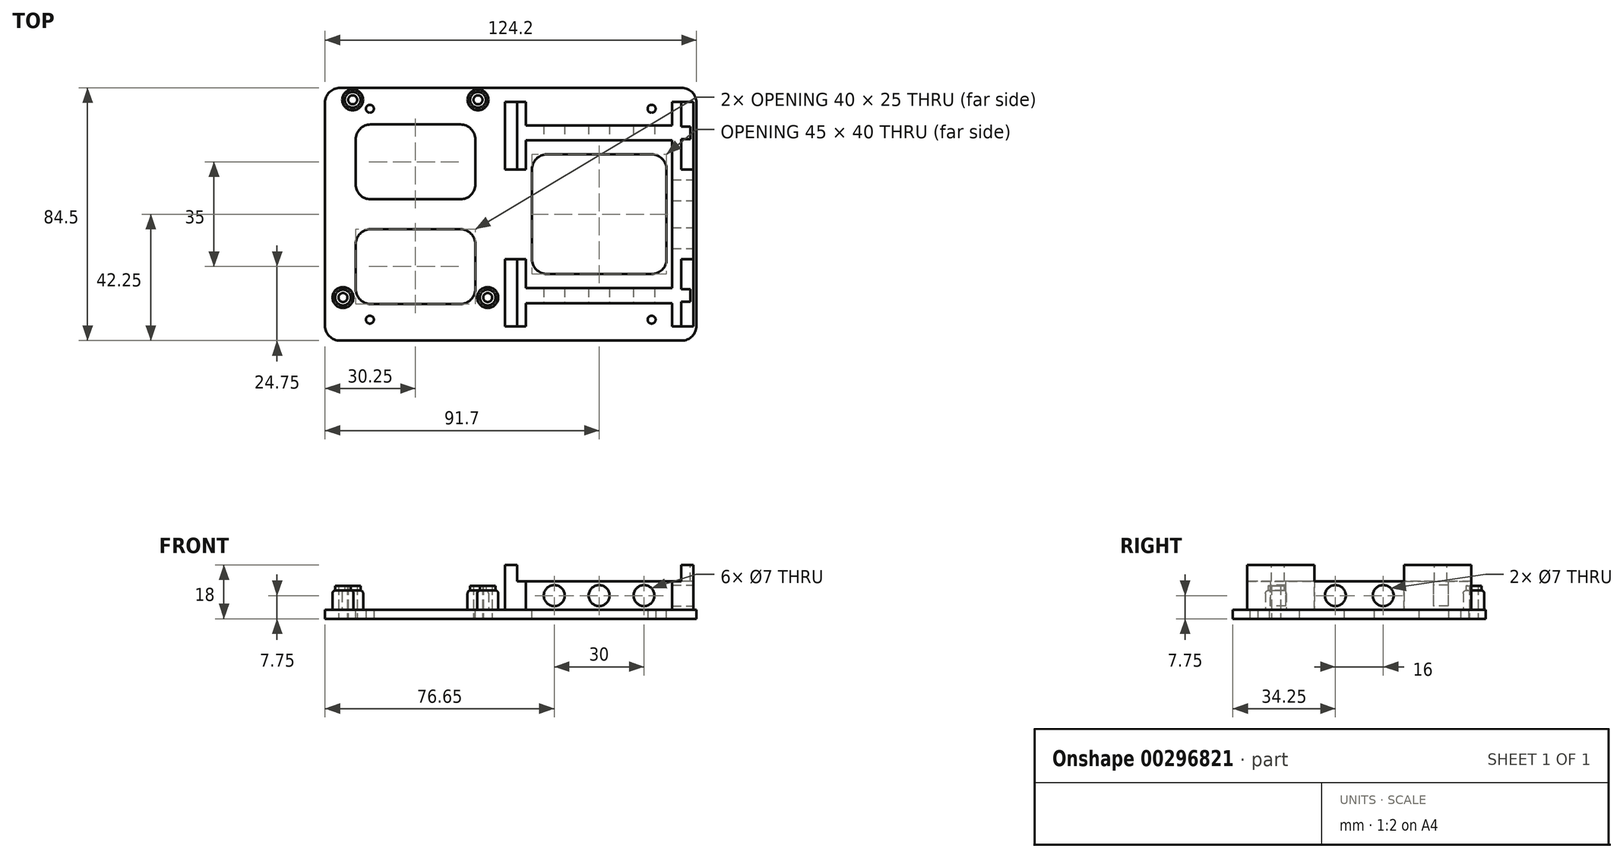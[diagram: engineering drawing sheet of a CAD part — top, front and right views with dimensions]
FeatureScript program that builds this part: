
annotation { "Feature Type Name" : "Feature", "Feature Type Description" : "" }
export const myFeature = defineFeature(function(context is Context, id is Id, definition is map)
    precondition{}
    {
        {
            var Q0;
            Q0=qCreatedBy(makeId("Top.planeOp"),FACE);
            var sketch = newSketch(context, id + "F0", { "sketchPlane" : qUnion([Q0])});
            skLineSegment(sketch, "E0", {"start": v(0, 0) * mm, "end": v(0, 35.25) * mm, "construction": true});
            skLineSegment(sketch, "E1", {"start": v(0, 35.25) * mm, "end": v(47.1, 35.25) * mm, "construction": true});
            skLineSegment(sketch, "E2", {"start": v(47.1, 35.25) * mm, "end": v(47.1, 0) * mm, "construction": true});
            skLineSegment(sketch, "E3", {"start": v(47.1, 0) * mm, "end": v(47.1, -35.25) * mm, "construction": true});
            skLineSegment(sketch, "E4", {"start": v(47.1, -35.25) * mm, "end": v(0, -35.25) * mm, "construction": true});
            skLineSegment(sketch, "E5", {"start": v(0, -35.25) * mm, "end": v(-47.1, -35.25) * mm, "construction": true});
            skLineSegment(sketch, "E6", {"start": v(-47.1, -35.25) * mm, "end": v(-47.1, 0) * mm, "construction": true});
            skLineSegment(sketch, "E7", {"start": v(-47.1, 0) * mm, "end": v(-47.1, 35.25) * mm, "construction": true});
            skLineSegment(sketch, "E8", {"start": v(-47.1, 35.25) * mm, "end": v(0, 35.25) * mm, "construction": true});
            skLineSegment(sketch, "E9", {"start": v(0, 0) * mm, "end": v(0, -35.25) * mm, "construction": true});
            skLineSegment(sketch, "E10", {"start": v(0, 0) * mm, "end": v(47.1, 0) * mm, "construction": true});
            skLineSegment(sketch, "E11", {"start": v(0, 0) * mm, "end": v(-47.1, 0) * mm, "construction": true});
            skCircle(sketch, "E12", {"center": v(-47.1, 35.25) * mm, "radius": 1.32 * mm});
            skCircle(sketch, "E13", {"center": v(-47.1, -35.25) * mm, "radius": 1.32 * mm});
            skCircle(sketch, "E14", {"center": v(47.1, -35.25) * mm, "radius": 1.32 * mm});
            skCircle(sketch, "E15", {"center": v(47.1, 35.25) * mm, "radius": 1.32 * mm});
            skLineSegment(sketch, "E16", {"start": v(0, 35.25) * mm, "end": v(0, 42.25) * mm, "construction": true});
            skLineSegment(sketch, "E17", {"start": v(0, -35.25) * mm, "end": v(0, -42.25) * mm, "construction": true});
            skLineSegment(sketch, "E18", {"start": v(0, 42.25) * mm, "end": v(57.1, 42.25) * mm});
            skLineSegment(sketch, "E19", {"start": v(62.1, 37.25) * mm, "end": v(62.1, 0) * mm});
            skLineSegment(sketch, "E20", {"start": v(62.1, 0) * mm, "end": v(62.1, -37.25) * mm});
            skLineSegment(sketch, "E21", {"start": v(57.1, -42.25) * mm, "end": v(0, -42.25) * mm});
            skLineSegment(sketch, "E22", {"start": v(0, -42.25) * mm, "end": v(-57.1, -42.25) * mm});
            skLineSegment(sketch, "E23", {"start": v(-62.1, -37.25) * mm, "end": v(-62.1, 0) * mm});
            skLineSegment(sketch, "E24", {"start": v(-62.1, 0) * mm, "end": v(-62.1, 37.25) * mm});
            skLineSegment(sketch, "E25", {"start": v(-57.1, 42.25) * mm, "end": v(0, 42.25) * mm});
            skLineSegment(sketch, "E26", {"start": v(-47.1, 0) * mm, "end": v(-62.1, 0) * mm, "construction": true});
            skLineSegment(sketch, "E27", {"start": v(47.1, 0) * mm, "end": v(62.1, 0) * mm, "construction": true});
            skPoint(sketch, "E28.visualSharp", {"position": v(-62.1, 42.25) * mm});
            skArc(sketch, "E28.filletArc", {"start": v(-57.1, 42.25) * mm, "mid": v(-60.64, 40.79) * mm, "end": v(-62.1, 37.25) * mm});
            skPoint(sketch, "E29.visualSharp", {"position": v(62.1, 42.25) * mm});
            skArc(sketch, "E29.filletArc", {"start": v(62.1, 37.25) * mm, "mid": v(60.64, 40.79) * mm, "end": v(57.1, 42.25) * mm});
            skPoint(sketch, "E30.visualSharp", {"position": v(62.1, -42.25) * mm});
            skArc(sketch, "E30.filletArc", {"start": v(57.1, -42.25) * mm, "mid": v(60.64, -40.79) * mm, "end": v(62.1, -37.25) * mm});
            skPoint(sketch, "E31.visualSharp", {"position": v(-62.1, -42.25) * mm});
            skArc(sketch, "E31.filletArc", {"start": v(-62.1, -37.25) * mm, "mid": v(-60.64, -40.79) * mm, "end": v(-57.1, -42.25) * mm});
            skSolve(sketch);
        }
        {
            var Q0;
            Q0 = qSketchRegion(id + "F0", true);
            extrude(context, id + "F1", {"entities" : qUnion([Q0]), "depth" : 3 * mm});
        }
        {
            var Q0;
            Q0=makeQuery(id+"F1.opExtrude","CAP_FACE",FACE,{"disambiguationData":[OSD([sQuery(id+"F0.wireOp",EDGE,"E12"),sQuery(id+"F0.wireOp",EDGE,"E13"),sQuery(id+"F0.wireOp",EDGE,"E14"),sQuery(id+"F0.wireOp",EDGE,"E15"),sQuery(id+"F0.wireOp",EDGE,"E18"),sQuery(id+"F0.wireOp",EDGE,"E19"),sQuery(id+"F0.wireOp",EDGE,"E20"),sQuery(id+"F0.wireOp",EDGE,"E21"),sQuery(id+"F0.wireOp",EDGE,"E22"),sQuery(id+"F0.wireOp",EDGE,"E23"),sQuery(id+"F0.wireOp",EDGE,"E24"),sQuery(id+"F0.wireOp",EDGE,"E25")])],"isStart":false});
            var sketch = newSketch(context, id + "F2", { "sketchPlane" : qUnion([Q0])});
            skLineSegment(sketch, "E32", {"start": v(-52.86, 38.25) * mm, "end": v(-10.95, 38.25) * mm, "construction": true});
            skLineSegment(sketch, "E33", {"start": v(-56.1, -27.85) * mm, "end": v(-7.7, -27.85) * mm, "construction": true});
            skCircle(sketch, "E34", {"center": v(-56.1, -27.85) * mm, "radius": 2.62 * mm});
            skCircle(sketch, "E35", {"center": v(-7.7, -27.85) * mm, "radius": 2.62 * mm});
            skCircle(sketch, "E36", {"center": v(-52.86, 38.25) * mm, "radius": 2.62 * mm});
            skCircle(sketch, "E37", {"center": v(-10.95, 38.25) * mm, "radius": 2.62 * mm});
            skCircle(sketch, "E38", {"center": v(-52.86, 38.25) * mm, "radius": 1.5 * mm});
            skCircle(sketch, "E39", {"center": v(-10.95, 38.25) * mm, "radius": 1.5 * mm});
            skCircle(sketch, "E40", {"center": v(-56.1, -27.85) * mm, "radius": 1.5 * mm});
            skCircle(sketch, "E41", {"center": v(-7.7, -27.85) * mm, "radius": 1.5 * mm});
            skLineSegment(sketch, "E42", {"start": v(-52.86, 38.25) * mm, "end": v(-52.86, -27.85) * mm, "construction": true});
            skLineSegment(sketch, "E43", {"start": v(-10.95, 38.25) * mm, "end": v(-10.95, -27.85) * mm, "construction": true});
            skSolve(sketch);
        }
        {
            var Q0;
            Q0 = qSketchRegion(id + "F2", true);
            extrude(context, id + "F3", {"entities" : qUnion([Q0]), "operationType" : NewBodyOperationType.ADD, "depth" : 8 * mm});
        }
        {
            var Q0;
            {var subQ0=sQuery(id+"F0.wireOp",EDGE,"E14");var subQ1=sQuery(id+"F0.wireOp",EDGE,"E24");var subQ2=sQuery(id+"F0.wireOp",EDGE,"E23");var subQ3=sQuery(id+"F0.wireOp",EDGE,"E22");var subQ4=sQuery(id+"F0.wireOp",EDGE,"E21");var subQ5=sQuery(id+"F0.wireOp",EDGE,"E20");var subQ6=sQuery(id+"F0.wireOp",EDGE,"E19");var subQ7=sQuery(id+"F0.wireOp",EDGE,"E25");var subQ8=sQuery(id+"F0.wireOp",EDGE,"E18");var subQ9=sQuery(id+"F0.wireOp",EDGE,"E12");var subQ10=sQuery(id+"F0.wireOp",EDGE,"E15");var subQ11=sQuery(id+"F0.wireOp",EDGE,"E13");Q0=makeQuery(id+"F3.boolean.opBoolean","SPLIT",FACE,{"disambiguationData":[TD([makeQuery(id+"F1.opExtrude","SWEPT_FACE",FACE,{"disambiguationData":[OSD([subQ9])]})])],"derivedFrom":makeQuery(id+"F1.opExtrude","CAP_FACE",FACE,{"disambiguationData":[OSD([subQ9,subQ11,subQ0,subQ10,subQ8,subQ6,subQ5,subQ4,subQ3,subQ2,subQ1,subQ7])],"isStart":false})});}
            var sketch = newSketch(context, id + "F4", { "sketchPlane" : qUnion([Q0])});
            skCircle(sketch, "E44", {"center": v(-10.95, 38.25) * mm, "radius": 3.5 * mm});
            skCircle(sketch, "E45", {"center": v(-7.7, -27.85) * mm, "radius": 3.5 * mm});
            skCircle(sketch, "E46", {"center": v(-56.1, -27.85) * mm, "radius": 3.5 * mm});
            skCircle(sketch, "E47", {"center": v(-52.86, 38.25) * mm, "radius": 3.5 * mm});
            skSolve(sketch);
        }
        {
            var Q0;
            Q0 = qSketchRegion(id + "F4", true);
            extrude(context, id + "F5", {"entities" : qUnion([Q0]), "operationType" : NewBodyOperationType.ADD, "depth" : 6.5 * mm});
        }
        {
            var Q0;
            {var subQ0=sQuery(id+"F0.wireOp",EDGE,"E14");var subQ1=sQuery(id+"F0.wireOp",EDGE,"E24");var subQ2=sQuery(id+"F0.wireOp",EDGE,"E23");var subQ3=sQuery(id+"F0.wireOp",EDGE,"E22");var subQ4=sQuery(id+"F0.wireOp",EDGE,"E21");var subQ5=sQuery(id+"F0.wireOp",EDGE,"E20");var subQ6=sQuery(id+"F0.wireOp",EDGE,"E19");var subQ7=sQuery(id+"F0.wireOp",EDGE,"E25");var subQ8=sQuery(id+"F0.wireOp",EDGE,"E18");var subQ9=sQuery(id+"F0.wireOp",EDGE,"E12");var subQ10=sQuery(id+"F0.wireOp",EDGE,"E15");var subQ11=sQuery(id+"F0.wireOp",EDGE,"E13");Q0=makeQuery(id+"F3.boolean.opBoolean","SPLIT",FACE,{"disambiguationData":[TD([makeQuery(id+"F1.opExtrude","SWEPT_FACE",FACE,{"disambiguationData":[OSD([subQ9])]})])],"derivedFrom":makeQuery(id+"F1.opExtrude","CAP_FACE",FACE,{"disambiguationData":[OSD([subQ9,subQ11,subQ0,subQ10,subQ8,subQ6,subQ5,subQ4,subQ3,subQ2,subQ1,subQ7])],"isStart":false})});}
            var sketch = newSketch(context, id + "F6", { "sketchPlane" : qUnion([Q0])});
            skLineSegment(sketch, "E48", {"start": v(2.1, 0) * mm, "end": v(2.1, 37.5) * mm, "construction": true});
            skLineSegment(sketch, "E49", {"start": v(2.1, 0) * mm, "end": v(2.1, -37.5) * mm, "construction": true});
            skLineSegment(sketch, "E50", {"start": v(57, 0) * mm, "end": v(57, 37.5) * mm, "construction": true});
            skLineSegment(sketch, "E51", {"start": v(57, 0) * mm, "end": v(57, -37.5) * mm, "construction": true});
            skLineSegment(sketch, "E52", {"start": v(2.1, 37.5) * mm, "end": v(57, 37.5) * mm, "construction": true});
            skLineSegment(sketch, "E53", {"start": v(2.1, 37.5) * mm, "end": v(-1.9, 37.5) * mm});
            skLineSegment(sketch, "E54", {"start": v(-1.9, 37.5) * mm, "end": v(-1.9, -37.5) * mm});
            skLineSegment(sketch, "E55", {"start": v(-1.9, -37.5) * mm, "end": v(2.1, -37.5) * mm});
            skLineSegment(sketch, "E56", {"start": v(2.1, 37.5) * mm, "end": v(5.1, 37.5) * mm});
            skLineSegment(sketch, "E57", {"start": v(5.1, 37.5) * mm, "end": v(5.1, -37.5) * mm});
            skLineSegment(sketch, "E58", {"start": v(5.1, -37.5) * mm, "end": v(2.1, -37.5) * mm});
            skLineSegment(sketch, "E59", {"start": v(57, 37.5) * mm, "end": v(54, 37.5) * mm});
            skLineSegment(sketch, "E60", {"start": v(57, 37.5) * mm, "end": v(61, 37.5) * mm});
            skLineSegment(sketch, "E61", {"start": v(54, 37.5) * mm, "end": v(54, -37.5) * mm});
            skLineSegment(sketch, "E62", {"start": v(54, -37.5) * mm, "end": v(57, -37.5) * mm});
            skLineSegment(sketch, "E63", {"start": v(57, -37.5) * mm, "end": v(61, -37.5) * mm});
            skLineSegment(sketch, "E64", {"start": v(61, -37.5) * mm, "end": v(61, 37.5) * mm});
            skSolve(sketch);
        }
        {
            var Q0;
            Q0=makeQuery(id+"F6.imprint","IMPRINT",FACE,{"disambiguationData":[TD([[makeQuery(id+"F6.imprint","IMPRINT",EDGE,{"derivedFrom":sQuery(id+"F6.wireOp",EDGE,"E53")}),1.0]])]});
            var Q1;
            Q1=makeQuery(id+"F6.imprint","IMPRINT",FACE,{"disambiguationData":[TD([[makeQuery(id+"F6.imprint","IMPRINT",EDGE,{"derivedFrom":sQuery(id+"F6.wireOp",EDGE,"E59")}),1.0]])]});
            extrude(context, id + "F7", {"entities" : qUnion([Q0, Q1]), "operationType" : NewBodyOperationType.ADD, "depth" : 7.5 * mm});
        }
        {
            var Q0;
            Q0=makeQuery(id+"F7.opExtrude","CAP_FACE",FACE,{"disambiguationData":[OSD([sQuery(id+"F6.wireOp",EDGE,"E53"),sQuery(id+"F6.wireOp",EDGE,"E54"),sQuery(id+"F6.wireOp",EDGE,"E55"),sQuery(id+"F6.wireOp",EDGE,"E56"),sQuery(id+"F6.wireOp",EDGE,"E57"),sQuery(id+"F6.wireOp",EDGE,"E58")])],"isStart":false});
            var sketch = newSketch(context, id + "F8", { "sketchPlane" : qUnion([Q0])});
            skLineSegment(sketch, "E65.bottom", {"start": v(-1.9, -37.5) * mm, "end": v(2.1, -37.5) * mm});
            skLineSegment(sketch, "E65.top", {"start": v(-1.9, 37.5) * mm, "end": v(2.1, 37.5) * mm});
            skLineSegment(sketch, "E65.left", {"start": v(-1.9, -37.5) * mm, "end": v(-1.9, 37.5) * mm});
            skLineSegment(sketch, "E65.right", {"start": v(2.1, -37.5) * mm, "end": v(2.1, 37.5) * mm});
            skSolve(sketch);
        }
        {
            var Q0;
            Q0 = qSketchRegion(id + "F8", true);
            extrude(context, id + "F9", {"entities" : qUnion([Q0]), "operationType" : NewBodyOperationType.ADD, "depth" : 10 * mm});
        }
        {
            var Q0;
            Q0=makeQuery(id+"F7.opExtrude","CAP_FACE",FACE,{"disambiguationData":[OSD([sQuery(id+"F6.wireOp",EDGE,"E59"),sQuery(id+"F6.wireOp",EDGE,"E60"),sQuery(id+"F6.wireOp",EDGE,"E61"),sQuery(id+"F6.wireOp",EDGE,"E62"),sQuery(id+"F6.wireOp",EDGE,"E63"),sQuery(id+"F6.wireOp",EDGE,"E64")])],"isStart":false});
            var sketch = newSketch(context, id + "F10", { "sketchPlane" : qUnion([Q0])});
            skLineSegment(sketch, "E66.bottom", {"start": v(61, 37.5) * mm, "end": v(57, 37.5) * mm});
            skLineSegment(sketch, "E66.top", {"start": v(61, -37.5) * mm, "end": v(57, -37.5) * mm});
            skLineSegment(sketch, "E66.left", {"start": v(61, 37.5) * mm, "end": v(61, -37.5) * mm});
            skLineSegment(sketch, "E66.right", {"start": v(57, 37.5) * mm, "end": v(57, -37.5) * mm});
            skSolve(sketch);
        }
        {
            var Q0;
            Q0 = qSketchRegion(id + "F10", true);
            extrude(context, id + "F11", {"entities" : qUnion([Q0]), "operationType" : NewBodyOperationType.ADD, "depth" : 10 * mm});
        }
        {
            var Q0;
            Q0=makeQuery(id+"F11.opExtrude","CAP_FACE",FACE,{"disambiguationData":[OSD([sQuery(id+"F10.wireOp",EDGE,"E66.bottom"),sQuery(id+"F10.wireOp",EDGE,"E66.top"),sQuery(id+"F10.wireOp",EDGE,"E66.left"),sQuery(id+"F10.wireOp",EDGE,"E66.right")])],"isStart":false});
            var sketch = newSketch(context, id + "F12", { "sketchPlane" : qUnion([Q0])});
            skPoint(sketch, "E67.startSnap0", {"position": v(61, 0) * mm});
            skLineSegment(sketch, "E68", {"start": v(60, 29.3) * mm, "end": v(57, 29.3) * mm});
            skLineSegment(sketch, "E69", {"start": v(57, 29.3) * mm, "end": v(57, 25.1) * mm});
            skLineSegment(sketch, "E70", {"start": v(57, 25.1) * mm, "end": v(60, 25.1) * mm});
            skLineSegment(sketch, "E71", {"start": v(60, -29.3) * mm, "end": v(57, -29.3) * mm});
            skLineSegment(sketch, "E72", {"start": v(57, -29.3) * mm, "end": v(57, -25.1) * mm});
            skLineSegment(sketch, "E73", {"start": v(57, -25.1) * mm, "end": v(60, -25.1) * mm});
            skLineSegment(sketch, "E74", {"start": v(60, -25.1) * mm, "end": v(60, -27.2) * mm});
            skLineSegment(sketch, "E75", {"start": v(60, -27.2) * mm, "end": v(60, -29.3) * mm});
            skLineSegment(sketch, "E76", {"start": v(60, 25.1) * mm, "end": v(60, 27.2) * mm});
            skLineSegment(sketch, "E77", {"start": v(60, 29.3) * mm, "end": v(60, 27.2) * mm});
            skLineSegment(sketch, "E78", {"start": v(60, 27.2) * mm, "end": v(57, 27.2) * mm, "construction": true});
            skLineSegment(sketch, "E79", {"start": v(58.5, 27.2) * mm, "end": v(58.5, 0) * mm, "construction": true});
            skLineSegment(sketch, "E80", {"start": v(57, -27.2) * mm, "end": v(60, -27.2) * mm, "construction": true});
            skLineSegment(sketch, "E81", {"start": v(58.5, -27.2) * mm, "end": v(58.5, 0) * mm, "construction": true});
            skSolve(sketch);
        }
        {
            var Q0;
            Q0=makeQuery(id+"F12.imprint","IMPRINT",FACE,{"disambiguationData":[TD([[makeQuery(id+"F12.imprint","IMPRINT",EDGE,{"derivedFrom":sQuery(id+"F12.wireOp",EDGE,"E71")}),-1.0]])]});
            var Q1;
            Q1=makeQuery(id+"F12.imprint","IMPRINT",FACE,{"disambiguationData":[TD([[makeQuery(id+"F12.imprint","IMPRINT",EDGE,{"derivedFrom":sQuery(id+"F12.wireOp",EDGE,"E68")}),1.0]])]});
            extrude(context, id + "F13", {"entities" : qUnion([Q0, Q1]), "operationType" : NewBodyOperationType.REMOVE, "oppositeDirection" : true, "depth" : 10 * mm});
        }
        {
            var Q0;
            Q0=makeQuery(id+"F9.boolean.opBoolean","MERGE",FACE,{"derivedFrom":[makeQuery(id+"F7.opExtrude","SWEPT_FACE",FACE,{"disambiguationData":[OSD([sQuery(id+"F6.wireOp",EDGE,"E54")])]}),makeQuery(id+"F9.opExtrude","SWEPT_FACE",FACE,{"disambiguationData":[OSD([sQuery(id+"F8.wireOp",EDGE,"E65.left")])]})]});
            var sketch = newSketch(context, id + "F14", { "sketchPlane" : qUnion([Q0])});
            skLineSegment(sketch, "E82.bottom", {"start": v(-15, 20.5) * mm, "end": v(15, 20.5) * mm});
            skLineSegment(sketch, "E82.top", {"start": v(-15, 3) * mm, "end": v(15, 3) * mm});
            skLineSegment(sketch, "E82.left", {"start": v(-15, 20.5) * mm, "end": v(-15, 3) * mm});
            skLineSegment(sketch, "E82.right", {"start": v(15, 20.5) * mm, "end": v(15, 3) * mm});
            skSolve(sketch);
        }
        {
            var Q0;
            Q0 = qSketchRegion(id + "F14", true);
            extrude(context, id + "F15", {"entities" : qUnion([Q0]), "operationType" : NewBodyOperationType.REMOVE, "endBound" : BoundingType.THROUGH_ALL, "oppositeDirection" : true, "depth" : 25 * mm});
        }
        {
            var Q0;
            Q0=makeQuery(id+"F9.boolean.opBoolean","MERGE",FACE,{"derivedFrom":[makeQuery(id+"F7.opExtrude","SWEPT_FACE",FACE,{"disambiguationData":[OSD([sQuery(id+"F6.wireOp",EDGE,"E55"),sQuery(id+"F6.wireOp",EDGE,"E58")])]}),makeQuery(id+"F9.opExtrude","SWEPT_FACE",FACE,{"disambiguationData":[OSD([sQuery(id+"F8.wireOp",EDGE,"E65.bottom")])]})]});
            var sketch = newSketch(context, id + "F16", { "sketchPlane" : qUnion([Q0])});
            skLineSegment(sketch, "E83.bottom", {"start": v(-1.9, 20.5) * mm, "end": v(2.1, 20.5) * mm});
            skLineSegment(sketch, "E83.top", {"start": v(-1.9, 18) * mm, "end": v(2.1, 18) * mm});
            skLineSegment(sketch, "E83.left", {"start": v(-1.9, 20.5) * mm, "end": v(-1.9, 18) * mm});
            skLineSegment(sketch, "E83.right", {"start": v(2.1, 20.5) * mm, "end": v(2.1, 18) * mm});
            skSolve(sketch);
        }
        {
            var Q0;
            Q0 = qSketchRegion(id + "F16", true);
            extrude(context, id + "F17", {"entities" : qUnion([Q0]), "operationType" : NewBodyOperationType.REMOVE, "endBound" : BoundingType.THROUGH_ALL, "oppositeDirection" : true, "depth" : 25 * mm});
        }
        {
            var Q0;
            {var subQ0=sQuery(id+"F0.wireOp",EDGE,"E28.filletArc");var subQ1=sQuery(id+"F0.wireOp",EDGE,"E24");var subQ2=sQuery(id+"F0.wireOp",EDGE,"E23");var subQ3=sQuery(id+"F0.wireOp",EDGE,"E22");var subQ4=sQuery(id+"F0.wireOp",EDGE,"E21");var subQ5=sQuery(id+"F0.wireOp",EDGE,"E20");var subQ6=sQuery(id+"F0.wireOp",EDGE,"E19");var subQ7=sQuery(id+"F0.wireOp",EDGE,"E25");var subQ8=sQuery(id+"F0.wireOp",EDGE,"E18");var subQ9=sQuery(id+"F0.wireOp",EDGE,"E29.filletArc");var subQ10=sQuery(id+"F0.wireOp",EDGE,"E12");var subQ11=sQuery(id+"F0.wireOp",EDGE,"E15");var subQ12=sQuery(id+"F0.wireOp",EDGE,"E13");var subQ13=sQuery(id+"F0.wireOp",EDGE,"E14");var subQ14=sQuery(id+"F0.wireOp",EDGE,"E30.filletArc");var subQ15=sQuery(id+"F0.wireOp",EDGE,"E31.filletArc");Q0=makeQuery(id+"F15.boolean.opBoolean","MERGE",FACE,{"derivedFrom":[makeQuery(id+"F3.boolean.opBoolean","SPLIT",FACE,{"disambiguationData":[TD([makeQuery(id+"F1.opExtrude","SWEPT_FACE",FACE,{"disambiguationData":[OSD([subQ10])]})])],"derivedFrom":makeQuery(id+"F1.opExtrude","CAP_FACE",FACE,{"disambiguationData":[OSD([subQ10,subQ12,subQ13,subQ11,subQ8,subQ6,subQ5,subQ4,subQ3,subQ2,subQ1,subQ7,subQ0,subQ9,subQ14,subQ15])],"isStart":false})}),makeQuery(id+"F15.opExtrude","SWEPT_FACE",FACE,{"disambiguationData":[OSD([sQuery(id+"F14.wireOp",EDGE,"E82.top")])]})]});}
            var sketch = newSketch(context, id + "F18", { "sketchPlane" : qUnion([Q0])});
            skLineSegment(sketch, "E84.bottom", {"start": v(5.1, -24.7) * mm, "end": v(54, -24.7) * mm});
            skLineSegment(sketch, "E84.top", {"start": v(5.1, -29.7) * mm, "end": v(54, -29.7) * mm});
            skLineSegment(sketch, "E84.left", {"start": v(5.1, -24.7) * mm, "end": v(5.1, -29.7) * mm});
            skLineSegment(sketch, "E84.right", {"start": v(54, -24.7) * mm, "end": v(54, -29.7) * mm});
            skLineSegment(sketch, "E85.bottom", {"start": v(5.1, 24.7) * mm, "end": v(54, 24.7) * mm});
            skLineSegment(sketch, "E85.top", {"start": v(5.1, 29.7) * mm, "end": v(54, 29.7) * mm});
            skLineSegment(sketch, "E85.left", {"start": v(5.1, 24.7) * mm, "end": v(5.1, 29.7) * mm});
            skLineSegment(sketch, "E85.right", {"start": v(54, 24.7) * mm, "end": v(54, 29.7) * mm});
            skSolve(sketch);
        }
        {
            var Q0;
            {var subQ0=sQuery(id+"F0.wireOp",EDGE,"E28.filletArc");var subQ1=sQuery(id+"F0.wireOp",EDGE,"E24");var subQ2=sQuery(id+"F0.wireOp",EDGE,"E23");var subQ3=sQuery(id+"F0.wireOp",EDGE,"E22");var subQ4=sQuery(id+"F0.wireOp",EDGE,"E21");var subQ5=sQuery(id+"F0.wireOp",EDGE,"E20");var subQ6=sQuery(id+"F0.wireOp",EDGE,"E19");var subQ7=sQuery(id+"F0.wireOp",EDGE,"E25");var subQ8=sQuery(id+"F0.wireOp",EDGE,"E18");var subQ9=sQuery(id+"F0.wireOp",EDGE,"E29.filletArc");var subQ10=sQuery(id+"F0.wireOp",EDGE,"E12");var subQ11=sQuery(id+"F0.wireOp",EDGE,"E15");var subQ12=sQuery(id+"F0.wireOp",EDGE,"E13");var subQ13=sQuery(id+"F0.wireOp",EDGE,"E14");var subQ14=sQuery(id+"F0.wireOp",EDGE,"E30.filletArc");var subQ15=sQuery(id+"F0.wireOp",EDGE,"E31.filletArc");Q0=makeQuery(id+"F15.boolean.opBoolean","MERGE",FACE,{"derivedFrom":[makeQuery(id+"F3.boolean.opBoolean","SPLIT",FACE,{"disambiguationData":[TD([makeQuery(id+"F1.opExtrude","SWEPT_FACE",FACE,{"disambiguationData":[OSD([subQ10])]})])],"derivedFrom":makeQuery(id+"F1.opExtrude","CAP_FACE",FACE,{"disambiguationData":[OSD([subQ10,subQ12,subQ13,subQ11,subQ8,subQ6,subQ5,subQ4,subQ3,subQ2,subQ1,subQ7,subQ0,subQ9,subQ14,subQ15])],"isStart":false})}),makeQuery(id+"F15.opExtrude","SWEPT_FACE",FACE,{"disambiguationData":[OSD([sQuery(id+"F14.wireOp",EDGE,"E82.top")])]})]});}
            var sketch = newSketch(context, id + "F19", { "sketchPlane" : qUnion([Q0])});
            skLineSegment(sketch, "E86.bottom", {"start": v(12.1, 20) * mm, "end": v(47.1, 20) * mm});
            skLineSegment(sketch, "E86.top", {"start": v(12.1, -20) * mm, "end": v(47.1, -20) * mm});
            skLineSegment(sketch, "E86.left", {"start": v(7.1, 15) * mm, "end": v(7.1, -15) * mm});
            skLineSegment(sketch, "E86.right", {"start": v(52.1, 15) * mm, "end": v(52.1, -15) * mm});
            skPoint(sketch, "E87.visualSharp", {"position": v(52.1, 20) * mm});
            skArc(sketch, "E87.filletArc", {"start": v(52.1, 15) * mm, "mid": v(50.64, 18.54) * mm, "end": v(47.1, 20) * mm});
            skPoint(sketch, "E88.visualSharp", {"position": v(52.1, -20) * mm});
            skArc(sketch, "E88.filletArc", {"start": v(47.1, -20) * mm, "mid": v(50.64, -18.54) * mm, "end": v(52.1, -15) * mm});
            skPoint(sketch, "E89.visualSharp", {"position": v(7.1, -20) * mm});
            skArc(sketch, "E89.filletArc", {"start": v(7.1, -15) * mm, "mid": v(8.56, -18.54) * mm, "end": v(12.1, -20) * mm});
            skPoint(sketch, "E90.visualSharp", {"position": v(7.1, 20) * mm});
            skArc(sketch, "E90.filletArc", {"start": v(12.1, 20) * mm, "mid": v(8.56, 18.54) * mm, "end": v(7.1, 15) * mm});
            skSolve(sketch);
        }
        {
            var Q0;
            Q0 = qSketchRegion(id + "F19", true);
            extrude(context, id + "F20", {"entities" : qUnion([Q0]), "operationType" : NewBodyOperationType.REMOVE, "endBound" : BoundingType.THROUGH_ALL, "oppositeDirection" : true, "depth" : 25 * mm});
        }
        {
            var Q0;
            Q0 = qSketchRegion(id + "F18", true);
            extrude(context, id + "F21", {"entities" : qUnion([Q0]), "operationType" : NewBodyOperationType.ADD, "depth" : 7.5 * mm});
        }
        {
            var Q0;
            {var subQ0=sQuery(id+"F0.wireOp",EDGE,"E28.filletArc");var subQ1=sQuery(id+"F0.wireOp",EDGE,"E24");var subQ2=sQuery(id+"F0.wireOp",EDGE,"E23");var subQ3=sQuery(id+"F0.wireOp",EDGE,"E22");var subQ4=sQuery(id+"F0.wireOp",EDGE,"E21");var subQ5=sQuery(id+"F0.wireOp",EDGE,"E20");var subQ6=sQuery(id+"F0.wireOp",EDGE,"E19");var subQ7=sQuery(id+"F0.wireOp",EDGE,"E25");var subQ8=sQuery(id+"F0.wireOp",EDGE,"E18");var subQ9=sQuery(id+"F0.wireOp",EDGE,"E29.filletArc");var subQ10=sQuery(id+"F0.wireOp",EDGE,"E12");var subQ11=sQuery(id+"F0.wireOp",EDGE,"E15");var subQ12=sQuery(id+"F0.wireOp",EDGE,"E13");var subQ13=sQuery(id+"F0.wireOp",EDGE,"E14");var subQ14=sQuery(id+"F0.wireOp",EDGE,"E30.filletArc");var subQ15=sQuery(id+"F0.wireOp",EDGE,"E31.filletArc");Q0=makeQuery(id+"F15.boolean.opBoolean","MERGE",FACE,{"derivedFrom":[makeQuery(id+"F3.boolean.opBoolean","SPLIT",FACE,{"disambiguationData":[TD([makeQuery(id+"F1.opExtrude","SWEPT_FACE",FACE,{"disambiguationData":[OSD([subQ10])]})])],"derivedFrom":makeQuery(id+"F1.opExtrude","CAP_FACE",FACE,{"disambiguationData":[OSD([subQ10,subQ12,subQ13,subQ11,subQ8,subQ6,subQ5,subQ4,subQ3,subQ2,subQ1,subQ7,subQ0,subQ9,subQ14,subQ15])],"isStart":false})}),makeQuery(id+"F15.opExtrude","SWEPT_FACE",FACE,{"disambiguationData":[OSD([sQuery(id+"F14.wireOp",EDGE,"E82.top")])]})]});}
            var sketch = newSketch(context, id + "F22", { "sketchPlane" : qUnion([Q0])});
            skLineSegment(sketch, "E91.bottom", {"start": v(-46.85, 30) * mm, "end": v(-16.85, 30) * mm});
            skLineSegment(sketch, "E91.top", {"start": v(-46.85, 5) * mm, "end": v(-16.85, 5) * mm});
            skLineSegment(sketch, "E91.left", {"start": v(-51.85, 25) * mm, "end": v(-51.85, 10) * mm});
            skLineSegment(sketch, "E91.right", {"start": v(-11.85, 25) * mm, "end": v(-11.85, 10) * mm});
            skPoint(sketch, "E92.visualSharp", {"position": v(-51.85, 30) * mm});
            skArc(sketch, "E92.filletArc", {"start": v(-46.85, 30) * mm, "mid": v(-50.39, 28.54) * mm, "end": v(-51.85, 25) * mm});
            skPoint(sketch, "E93.visualSharp", {"position": v(-11.85, 30) * mm});
            skArc(sketch, "E93.filletArc", {"start": v(-11.85, 25) * mm, "mid": v(-13.31, 28.54) * mm, "end": v(-16.85, 30) * mm});
            skPoint(sketch, "E94.visualSharp", {"position": v(-51.85, 5) * mm});
            skArc(sketch, "E94.filletArc", {"start": v(-51.85, 10) * mm, "mid": v(-50.39, 6.46) * mm, "end": v(-46.85, 5) * mm});
            skPoint(sketch, "E95.visualSharp", {"position": v(-11.85, 5) * mm});
            skArc(sketch, "E95.filletArc", {"start": v(-16.85, 5) * mm, "mid": v(-13.31, 6.46) * mm, "end": v(-11.85, 10) * mm});
            skLineSegment(sketch, "E96.bottom", {"start": v(-16.85, -30) * mm, "end": v(-46.85, -30) * mm});
            skLineSegment(sketch, "E96.top", {"start": v(-16.85, -5) * mm, "end": v(-46.85, -5) * mm});
            skLineSegment(sketch, "E96.left", {"start": v(-11.85, -25) * mm, "end": v(-11.85, -10) * mm});
            skLineSegment(sketch, "E96.right", {"start": v(-51.85, -25) * mm, "end": v(-51.85, -10) * mm});
            skPoint(sketch, "E97.visualSharp", {"position": v(-11.85, -30) * mm});
            skArc(sketch, "E97.filletArc", {"start": v(-16.85, -30) * mm, "mid": v(-13.31, -28.54) * mm, "end": v(-11.85, -25) * mm});
            skPoint(sketch, "E98.visualSharp", {"position": v(-11.85, -5) * mm});
            skArc(sketch, "E98.filletArc", {"start": v(-11.85, -10) * mm, "mid": v(-13.31, -6.46) * mm, "end": v(-16.85, -5) * mm});
            skPoint(sketch, "E99.visualSharp", {"position": v(-51.85, -5) * mm});
            skArc(sketch, "E99.filletArc", {"start": v(-46.85, -5) * mm, "mid": v(-50.39, -6.46) * mm, "end": v(-51.85, -10) * mm});
            skPoint(sketch, "E100.visualSharp", {"position": v(-51.85, -30) * mm});
            skArc(sketch, "E100.filletArc", {"start": v(-51.85, -25) * mm, "mid": v(-50.39, -28.54) * mm, "end": v(-46.85, -30) * mm});
            skSolve(sketch);
        }
        {
            var Q0;
            Q0 = qSketchRegion(id + "F22", true);
            extrude(context, id + "F23", {"entities" : qUnion([Q0]), "operationType" : NewBodyOperationType.REMOVE, "endBound" : BoundingType.THROUGH_ALL, "oppositeDirection" : true, "depth" : 25 * mm});
        }
        {
            var Q0;
            Q0=makeQuery(id+"F11.boolean.opBoolean","MERGE",FACE,{"derivedFrom":[makeQuery(id+"F7.opExtrude","SWEPT_FACE",FACE,{"disambiguationData":[OSD([sQuery(id+"F6.wireOp",EDGE,"E62"),sQuery(id+"F6.wireOp",EDGE,"E63")])]}),makeQuery(id+"F11.opExtrude","SWEPT_FACE",FACE,{"disambiguationData":[OSD([sQuery(id+"F10.wireOp",EDGE,"E66.top")])]})]});
            var sketch = newSketch(context, id + "F24", { "sketchPlane" : qUnion([Q0])});
            skLineSegment(sketch, "E101.bottom", {"start": v(57, 20.5) * mm, "end": v(61, 20.5) * mm});
            skLineSegment(sketch, "E101.top", {"start": v(57, 18) * mm, "end": v(61, 18) * mm});
            skLineSegment(sketch, "E101.left", {"start": v(57, 20.5) * mm, "end": v(57, 18) * mm});
            skLineSegment(sketch, "E101.right", {"start": v(61, 20.5) * mm, "end": v(61, 18) * mm});
            skSolve(sketch);
        }
        {
            var Q0;
            Q0 = qSketchRegion(id + "F24", true);
            extrude(context, id + "F25", {"entities" : qUnion([Q0]), "operationType" : NewBodyOperationType.REMOVE, "endBound" : BoundingType.THROUGH_ALL, "oppositeDirection" : true, "depth" : 25 * mm});
        }
        {
            var Q0;
            Q0=makeQuery(id+"F5.boolean.opBoolean","SPLIT",FACE,{"disambiguationData":[TD([makeQuery(id+"F3.opExtrude","SWEPT_FACE",FACE,{"disambiguationData":[OSD([sQuery(id+"F2.wireOp",EDGE,"E38")])]})])],"derivedFrom":makeQuery(id+"F5.opExtrude","CAP_FACE",FACE,{"disambiguationData":[OSD([sQuery(id+"F4.wireOp",EDGE,"E47")])],"isStart":false})});
            var Q1;
            Q1=makeQuery(id+"F5.boolean.opBoolean","SPLIT",FACE,{"disambiguationData":[TD([makeQuery(id+"F3.opExtrude","SWEPT_FACE",FACE,{"disambiguationData":[OSD([sQuery(id+"F2.wireOp",EDGE,"E39")])]})])],"derivedFrom":makeQuery(id+"F5.opExtrude","CAP_FACE",FACE,{"disambiguationData":[OSD([sQuery(id+"F4.wireOp",EDGE,"E44")])],"isStart":false})});
            var Q2;
            Q2=makeQuery(id+"F5.boolean.opBoolean","SPLIT",FACE,{"disambiguationData":[TD([makeQuery(id+"F3.opExtrude","SWEPT_FACE",FACE,{"disambiguationData":[OSD([sQuery(id+"F2.wireOp",EDGE,"E41")])]})])],"derivedFrom":makeQuery(id+"F5.opExtrude","CAP_FACE",FACE,{"disambiguationData":[OSD([sQuery(id+"F4.wireOp",EDGE,"E45")])],"isStart":false})});
            var Q3;
            Q3=makeQuery(id+"F5.boolean.opBoolean","SPLIT",FACE,{"disambiguationData":[TD([makeQuery(id+"F3.opExtrude","SWEPT_FACE",FACE,{"disambiguationData":[OSD([sQuery(id+"F2.wireOp",EDGE,"E40")])]})])],"derivedFrom":makeQuery(id+"F5.opExtrude","CAP_FACE",FACE,{"disambiguationData":[OSD([sQuery(id+"F4.wireOp",EDGE,"E46")])],"isStart":false})});
            extrude(context, id + "F26", {"entities" : qUnion([Q0, Q1, Q2, Q3]), "operationType" : NewBodyOperationType.REMOVE, "endBound" : BoundingType.THROUGH_ALL, "oppositeDirection" : true, "depth" : 25 * mm});
        }
        {
            var Q0;
            {var subQ0=sQuery(id+"F0.wireOp",EDGE,"E28.filletArc");var subQ1=sQuery(id+"F0.wireOp",EDGE,"E24");var subQ2=sQuery(id+"F0.wireOp",EDGE,"E23");var subQ3=sQuery(id+"F0.wireOp",EDGE,"E22");var subQ4=sQuery(id+"F0.wireOp",EDGE,"E21");var subQ5=sQuery(id+"F0.wireOp",EDGE,"E20");var subQ6=sQuery(id+"F0.wireOp",EDGE,"E19");var subQ7=sQuery(id+"F0.wireOp",EDGE,"E25");var subQ8=sQuery(id+"F0.wireOp",EDGE,"E18");var subQ9=sQuery(id+"F0.wireOp",EDGE,"E29.filletArc");var subQ10=sQuery(id+"F0.wireOp",EDGE,"E12");var subQ11=sQuery(id+"F0.wireOp",EDGE,"E15");var subQ12=sQuery(id+"F0.wireOp",EDGE,"E13");var subQ13=sQuery(id+"F0.wireOp",EDGE,"E14");var subQ14=sQuery(id+"F0.wireOp",EDGE,"E30.filletArc");var subQ15=sQuery(id+"F0.wireOp",EDGE,"E31.filletArc");Q0=makeQuery(id+"F15.boolean.opBoolean","MERGE",FACE,{"derivedFrom":[makeQuery(id+"F3.boolean.opBoolean","SPLIT",FACE,{"disambiguationData":[TD([makeQuery(id+"F1.opExtrude","SWEPT_FACE",FACE,{"disambiguationData":[OSD([subQ10])]})])],"derivedFrom":makeQuery(id+"F1.opExtrude","CAP_FACE",FACE,{"disambiguationData":[OSD([subQ10,subQ12,subQ13,subQ11,subQ8,subQ6,subQ5,subQ4,subQ3,subQ2,subQ1,subQ7,subQ0,subQ9,subQ14,subQ15])],"isStart":false})}),makeQuery(id+"F15.opExtrude","SWEPT_FACE",FACE,{"disambiguationData":[OSD([sQuery(id+"F14.wireOp",EDGE,"E82.top")])]})]});}
            var sketch = newSketch(context, id + "F27", { "sketchPlane" : qUnion([Q0])});
            skLineSegment(sketch, "E102.bottom", {"start": v(54, 15) * mm, "end": v(61, 15) * mm});
            skLineSegment(sketch, "E102.top", {"start": v(54, -15) * mm, "end": v(61, -15) * mm});
            skLineSegment(sketch, "E102.left", {"start": v(54, 15) * mm, "end": v(54, -15) * mm});
            skLineSegment(sketch, "E102.right", {"start": v(61, 15) * mm, "end": v(61, -15) * mm});
            skSolve(sketch);
        }
        {
            var Q0;
            Q0 = qSketchRegion(id + "F27", true);
            extrude(context, id + "F28", {"entities" : qUnion([Q0]), "operationType" : NewBodyOperationType.ADD, "depth" : 7.5 * mm});
        }
        {
            var Q0;
            Q0=makeQuery(id+"F5.opExtrude","CAP_EDGE",EDGE,{"disambiguationData":[OSD([sQuery(id+"F4.wireOp",EDGE,"E47")])],"isStart":false});
            var Q1;
            Q1=makeQuery(id+"F5.opExtrude","CAP_EDGE",EDGE,{"disambiguationData":[OSD([sQuery(id+"F4.wireOp",EDGE,"E44")])],"isStart":false});
            var Q2;
            Q2=makeQuery(id+"F5.opExtrude","CAP_EDGE",EDGE,{"disambiguationData":[OSD([sQuery(id+"F4.wireOp",EDGE,"E45")])],"isStart":false});
            var Q3;
            Q3=makeQuery(id+"F5.opExtrude","CAP_EDGE",EDGE,{"disambiguationData":[OSD([sQuery(id+"F4.wireOp",EDGE,"E46")])],"isStart":false});
            fillet(context, id + "F29", {"entities" : qUnion([Q0, Q1, Q2, Q3]), "radius" : 1 * mm, "tangentPropagation" : true, "allowEdgeOverflow" : false});
        }
        {
            var Q0;
            {var subQ1=sQuery(id+"F12.wireOp",EDGE,"E75");var subQ2=sQuery(id+"F12.wireOp",EDGE,"E74");var subQ3=sQuery(id+"F6.wireOp",EDGE,"E63");var subQ4=sQuery(id+"F6.wireOp",EDGE,"E62");var subQ5=sQuery(id+"F6.wireOp",EDGE,"E61");var subQ7=sQuery(id+"F12.wireOp",EDGE,"E71");var subQ8=sQuery(id+"F12.wireOp",EDGE,"E73");var subQ10=sQuery(id+"F12.wireOp",EDGE,"E77");var subQ11=sQuery(id+"F12.wireOp",EDGE,"E76");var subQ12=sQuery(id+"F12.wireOp",EDGE,"E70");var subQ13=sQuery(id+"F12.wireOp",EDGE,"E68");var subQ14=sQuery(id+"F6.wireOp",EDGE,"E60");var subQ15=sQuery(id+"F6.wireOp",EDGE,"E59");var subQ16=makeQuery(id+"F13.boolean.opBoolean","MERGE",FACE,{"derivedFrom":[makeQuery(id+"F7.opExtrude","CAP_FACE",FACE,{"disambiguationData":[OSD([subQ15,subQ14,subQ5,subQ4,subQ3,sQuery(id+"F6.wireOp",EDGE,"E64")])],"isStart":false}),makeQuery(id+"F13.opExtrude","CAP_FACE",FACE,{"disambiguationData":[OSD([subQ13,sQuery(id+"F12.wireOp",EDGE,"E69"),subQ12,subQ11,subQ10])],"isStart":false}),makeQuery(id+"F13.opExtrude","CAP_FACE",FACE,{"disambiguationData":[OSD([subQ7,sQuery(id+"F12.wireOp",EDGE,"E72"),subQ8,subQ2,subQ1])],"isStart":false})]});var subQ17=sQuery(id+"F6.wireOp",EDGE,"E57");var subQ20=sQuery(id+"F6.wireOp",EDGE,"E58");var subQ21=sQuery(id+"F6.wireOp",EDGE,"E55");var subQ22=sQuery(id+"F6.wireOp",EDGE,"E56");var subQ23=sQuery(id+"F6.wireOp",EDGE,"E53");var subQ24=makeQuery(id+"F7.opExtrude","CAP_FACE",FACE,{"disambiguationData":[OSD([subQ23,sQuery(id+"F6.wireOp",EDGE,"E54"),subQ21,subQ22,subQ17,subQ20])],"isStart":false});Q0=makeQuery(id+"F28.boolean.opBoolean","MERGE",FACE,{"derivedFrom":[makeQuery(id+"F21.boolean.opBoolean","MERGE",FACE,{"derivedFrom":[makeQuery(id+"F15.boolean.opBoolean","SPLIT",FACE,{"disambiguationData":[TD([makeQuery(id+"F9.opExtrude","SWEPT_FACE",FACE,{"disambiguationData":[OSD([sQuery(id+"F8.wireOp",EDGE,"E65.top")])]})])],"derivedFrom":subQ24}),makeQuery(id+"F15.boolean.opBoolean","SPLIT",FACE,{"disambiguationData":[TD([makeQuery(id+"F11.opExtrude","SWEPT_FACE",FACE,{"disambiguationData":[OSD([sQuery(id+"F10.wireOp",EDGE,"E66.bottom")])]})])],"derivedFrom":subQ16}),makeQuery(id+"F21.opExtrude","CAP_FACE",FACE,{"disambiguationData":[OSD([sQuery(id+"F18.wireOp",EDGE,"E85.bottom"),sQuery(id+"F18.wireOp",EDGE,"E85.top"),sQuery(id+"F18.wireOp",EDGE,"E85.left"),sQuery(id+"F18.wireOp",EDGE,"E85.right")])],"isStart":false})]}),makeQuery(id+"F21.boolean.opBoolean","MERGE",FACE,{"derivedFrom":[makeQuery(id+"F15.boolean.opBoolean","SPLIT",FACE,{"disambiguationData":[TD([makeQuery(id+"F9.opExtrude","SWEPT_FACE",FACE,{"disambiguationData":[OSD([sQuery(id+"F8.wireOp",EDGE,"E65.bottom")])]})])],"derivedFrom":subQ24}),makeQuery(id+"F15.boolean.opBoolean","SPLIT",FACE,{"disambiguationData":[TD([makeQuery(id+"F11.opExtrude","SWEPT_FACE",FACE,{"disambiguationData":[OSD([sQuery(id+"F10.wireOp",EDGE,"E66.top")])]})])],"derivedFrom":subQ16}),makeQuery(id+"F21.opExtrude","CAP_FACE",FACE,{"disambiguationData":[OSD([sQuery(id+"F18.wireOp",EDGE,"E84.bottom"),sQuery(id+"F18.wireOp",EDGE,"E84.top"),sQuery(id+"F18.wireOp",EDGE,"E84.left"),sQuery(id+"F18.wireOp",EDGE,"E84.right")])],"isStart":false})]}),makeQuery(id+"F28.opExtrude","CAP_FACE",FACE,{"disambiguationData":[OSD([sQuery(id+"F27.wireOp",EDGE,"E102.bottom"),sQuery(id+"F27.wireOp",EDGE,"E102.top"),sQuery(id+"F27.wireOp",EDGE,"E102.left"),sQuery(id+"F27.wireOp",EDGE,"E102.right")])],"isStart":false})]});}
            extrude(context, id + "F30", {"entities" : qUnion([Q0]), "operationType" : NewBodyOperationType.ADD, "depth" : 2 * mm});
        }
        {
            var Q0;
            {var subQ0=sQuery(id+"F18.wireOp",EDGE,"E84.top");Q0=makeQuery(id+"F30.boolean.opBoolean","MERGE",FACE,{"derivedFrom":[makeQuery(id+"F21.opExtrude","SWEPT_FACE",FACE,{"disambiguationData":[OSD([subQ0])]}),makeQuery(id+"F30.opExtrude","SWEPT_FACE",FACE,{"disambiguationData":[OSD([subQ0])]})]});}
            var sketch = newSketch(context, id + "F31", { "sketchPlane" : qUnion([Q0])});
            skCircle(sketch, "E103", {"center": v(29.55, 7.75) * mm, "radius": 3.5 * mm});
            skPoint(sketch, "E103.centerSnap0", {"position": v(29.55, 12.5) * mm});
            skPoint(sketch, "E103.centerSnap1", {"position": v(5.1, 7.75) * mm});
            skCircle(sketch, "E104", {"center": v(14.55, 7.75) * mm, "radius": 3.5 * mm});
            skCircle(sketch, "E105", {"center": v(44.55, 7.75) * mm, "radius": 3.5 * mm});
            skSolve(sketch);
        }
        {
            var Q0;
            Q0 = qSketchRegion(id + "F31", true);
            extrude(context, id + "F32", {"entities" : qUnion([Q0]), "operationType" : NewBodyOperationType.REMOVE, "endBound" : BoundingType.THROUGH_ALL, "oppositeDirection" : true, "depth" : 25 * mm});
        }
        {
            var Q0;
            {var subQ0=sQuery(id+"F27.wireOp",EDGE,"E102.right");var subQ1=sQuery(id+"F10.wireOp",EDGE,"E66.top");var subQ2=sQuery(id+"F10.wireOp",EDGE,"E66.left");var subQ3=sQuery(id+"F10.wireOp",EDGE,"E66.bottom");var subQ7=makeQuery(id+"F11.boolean.opBoolean","MERGE",FACE,{"derivedFrom":[makeQuery(id+"F7.opExtrude","SWEPT_FACE",FACE,{"disambiguationData":[OSD([sQuery(id+"F6.wireOp",EDGE,"E64")])]}),makeQuery(id+"F11.opExtrude","SWEPT_FACE",FACE,{"disambiguationData":[OSD([subQ2])]})]});Q0=makeQuery(id+"F30.boolean.opBoolean","MERGE",FACE,{"derivedFrom":[makeQuery(id+"F28.boolean.opBoolean","MERGE",FACE,{"derivedFrom":[makeQuery(id+"F15.boolean.opBoolean","SPLIT",FACE,{"disambiguationData":[TD([makeQuery(id+"F11.opExtrude","SWEPT_FACE",FACE,{"disambiguationData":[OSD([subQ3])]})])],"derivedFrom":subQ7}),makeQuery(id+"F15.boolean.opBoolean","SPLIT",FACE,{"disambiguationData":[TD([makeQuery(id+"F11.opExtrude","SWEPT_FACE",FACE,{"disambiguationData":[OSD([subQ1])]})])],"derivedFrom":subQ7}),makeQuery(id+"F28.opExtrude","SWEPT_FACE",FACE,{"disambiguationData":[OSD([subQ0])]})]}),makeQuery(id+"F30.opExtrude","SWEPT_FACE",FACE,{"disambiguationData":[OSD([subQ0])]})]});}
            var sketch = newSketch(context, id + "F33", { "sketchPlane" : qUnion([Q0])});
            skCircle(sketch, "E106", {"center": v(-8, 7.75) * mm, "radius": 3.5 * mm});
            skCircle(sketch, "E107", {"center": v(8, 7.75) * mm, "radius": 3.5 * mm});
            skSolve(sketch);
        }
        {
            var Q0;
            Q0 = qSketchRegion(id + "F33", true);
            extrude(context, id + "F34", {"entities" : qUnion([Q0]), "operationType" : NewBodyOperationType.REMOVE, "endBound" : BoundingType.THROUGH_ALL, "oppositeDirection" : true, "depth" : 25 * mm});
        }
    });
